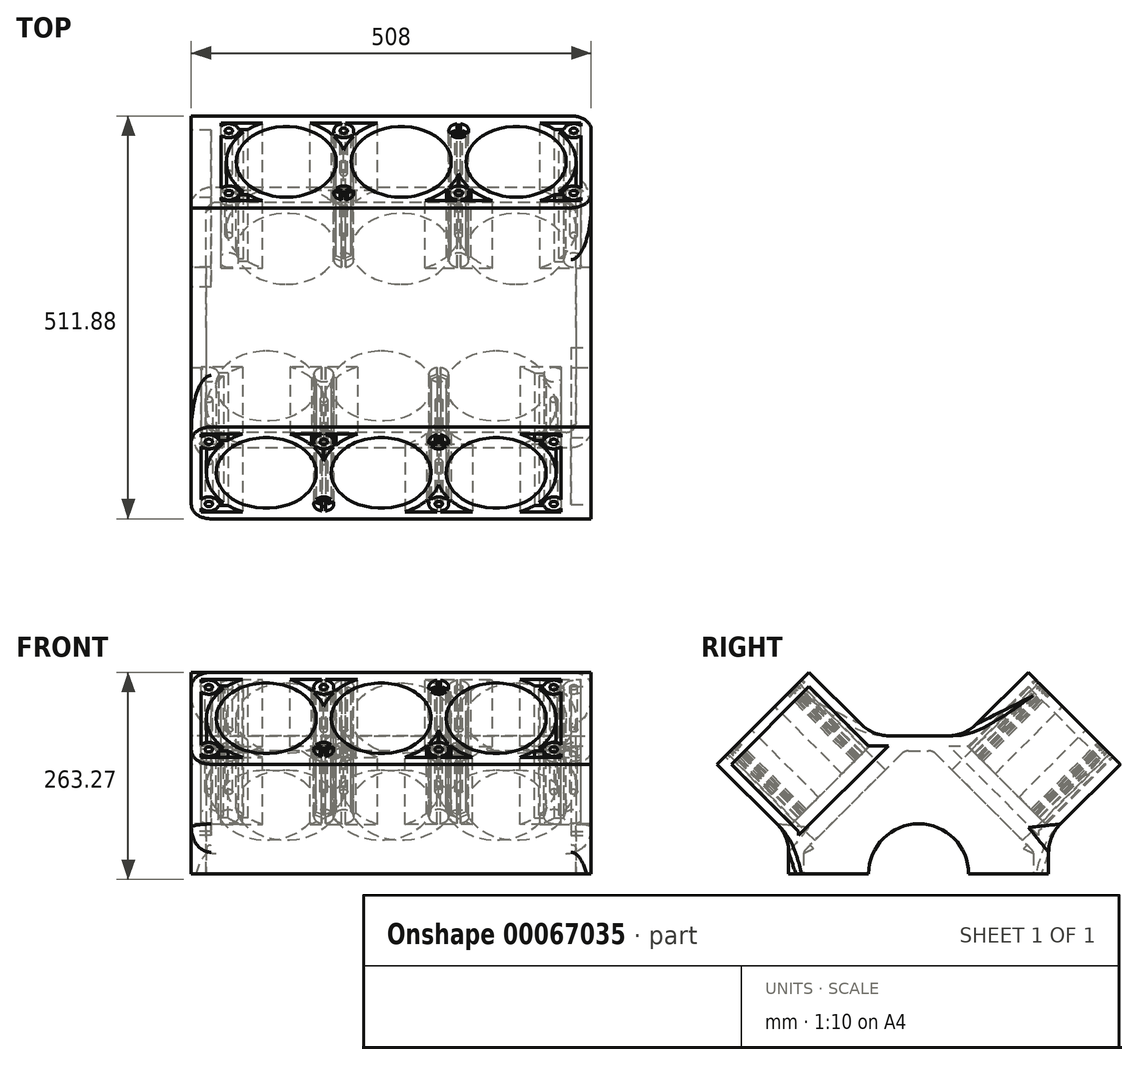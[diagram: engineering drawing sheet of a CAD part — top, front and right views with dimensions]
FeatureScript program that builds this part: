
annotation { "Feature Type Name" : "Feature", "Feature Type Description" : "" }
export const myFeature = defineFeature(function(context is Context, id is Id, definition is map)
    precondition{}
    {
        {
            var Q0;
            Q0=qCreatedBy(makeId("Right.planeOp"),FACE);
            var sketch = newSketch(context, id + "F0", { "sketchPlane" : qUnion([Q0])});
            skLineSegment(sketch, "E0", {"start": v(0, 175.36) * mm, "end": v(0, 0) * mm, "construction": true});
            skLineSegment(sketch, "E1", {"start": v(0, 0) * mm, "end": v(197.57, 197.57) * mm, "construction": true});
            skLineSegment(sketch, "E2", {"start": v(0, 175.36) * mm, "end": v(58.61, 175.36) * mm});
            skLineSegment(sketch, "E3", {"start": v(58.61, 175.36) * mm, "end": v(139.2, 255.94) * mm});
            skLineSegment(sketch, "E4", {"start": v(139.2, 255.94) * mm, "end": v(255.94, 139.2) * mm});
            skLineSegment(sketch, "E5", {"start": v(255.94, 139.2) * mm, "end": v(165.1, 48.36) * mm});
            skLineSegment(sketch, "E6", {"start": v(165.1, 48.36) * mm, "end": v(165.1, 0) * mm});
            skLineSegment(sketch, "E7", {"start": v(63.5, 0) * mm, "end": v(165.1, 0) * mm});
            skArc(sketch, "E8", {"start": v(0, 63.5) * mm, "mid": v(44.9, 44.9) * mm, "end": v(63.5, 0) * mm});
            skLineSegment(sketch, "E9", {"start": v(0, 175.36) * mm, "end": v(0, 63.5) * mm});
            skSolve(sketch);
        }
        {
            var Q0;
            Q0=qSketchRegion(id+"F0",true);
            extrude(context, id + "F1", {"entities" : qUnion([Q0]), "endBound" : BoundingType.SYMMETRIC, "depth" : 482.6 * mm});
        }
        {
            var Q0;
            Q0=makeQuery(id+"F1.opExtrude","SWEPT_FACE",FACE,{"disambiguationData":[OSD([sQuery(id+"F0.wireOp",EDGE,"E4")])]});
            var sketch = newSketch(context, id + "F2", { "sketchPlane" : qUnion([Q0])});
            skLineSegment(sketch, "E10", {"start": v(146.05, 0) * mm, "end": v(-146.05, 0) * mm, "construction": true});
            skCircle(sketch, "E11", {"center": v(146.05, 0) * mm, "radius": 63.5 * mm});
            skCircle(sketch, "E12", {"center": v(0, 0) * mm, "radius": 63.5 * mm});
            skCircle(sketch, "E13", {"center": v(-146.05, 0) * mm, "radius": 63.5 * mm});
            skSolve(sketch);
        }
        {
            var Q0;
            Q0=qSketchRegion(id+"F2",true);
            extrude(context, id + "F3", {"entities" : qUnion([Q0]), "operationType" : NewBodyOperationType.REMOVE, "endBound" : BoundingType.THROUGH_ALL, "oppositeDirection" : true, "depth" : 25.4 * mm});
        }
        {
            var Q0;
            Q0=makeQuery(id+"F1.opExtrude","SWEPT_FACE",FACE,{"disambiguationData":[OSD([sQuery(id+"F0.wireOp",EDGE,"E4")])]});
            var sketch = newSketch(context, id + "F4", { "sketchPlane" : qUnion([Q0])});
            skCircle(sketch, "E14", {"center": v(146.05, 0) * mm, "radius": 76 * mm});
            skCircle(sketch, "E15", {"center": v(0, 0) * mm, "radius": 76 * mm});
            skCircle(sketch, "E16", {"center": v(146.05, 0) * mm, "radius": 91.95 * mm, "construction": true});
            skCircle(sketch, "E17", {"center": v(73.03, -55.88) * mm, "radius": 12.7 * mm});
            skLineSegment(sketch, "E18", {"start": v(146.05, 0) * mm, "end": v(146.05, -169.57) * mm, "construction": true});
            skLineSegment(sketch, "E19", {"start": v(146.05, 0) * mm, "end": v(35.62, 0) * mm, "construction": true});
            skCircle(sketch, "E20.MirrorC", {"center": v(219.07, -55.88) * mm, "radius": 12.7 * mm});
            skCircle(sketch, "E21.MirrorC", {"center": v(73.03, 55.88) * mm, "radius": 12.7 * mm});
            skCircle(sketch, "E22.MirrorC", {"center": v(219.07, 55.88) * mm, "radius": 12.7 * mm});
            skLineSegment(sketch, "E23.bottom", {"start": v(228.6, -69.85) * mm, "end": v(-228.6, -69.85) * mm});
            skLineSegment(sketch, "E23.top", {"start": v(228.6, 69.85) * mm, "end": v(-228.6, 69.85) * mm});
            skLineSegment(sketch, "E23.left", {"start": v(228.6, -69.85) * mm, "end": v(228.6, 69.85) * mm});
            skLineSegment(sketch, "E23.right", {"start": v(-228.6, -69.85) * mm, "end": v(-228.6, 69.85) * mm});
            skLineSegment(sketch, "E24", {"start": v(0, -135.82) * mm, "end": v(0, 167.5) * mm, "construction": true});
            skCircle(sketch, "E25.MirrorC", {"center": v(-73.03, -55.88) * mm, "radius": 12.7 * mm});
            skCircle(sketch, "E26.MirrorC", {"center": v(-73.03, 55.88) * mm, "radius": 12.7 * mm});
            skCircle(sketch, "E27.MirrorC", {"center": v(-219.07, 55.88) * mm, "radius": 12.7 * mm});
            skCircle(sketch, "E28.MirrorC", {"center": v(-219.07, -55.88) * mm, "radius": 12.7 * mm});
            skCircle(sketch, "E29.MirrorC", {"center": v(-146.05, 0) * mm, "radius": 76 * mm});
            skSolve(sketch);
        }
        {
            var Q0;
            {var subQ9=sQuery(id+"F4.wireOp",EDGE,"E14");var subQ11=sQuery(id+"F4.wireOp",EDGE,"E23.top");var subQ12=makeQuery(id+"F4.imprint","INTERSECT",VERTEX,{"disambiguationData":[OD(1.0)],"derivedFrom":[subQ9,subQ11]});Q0=makeQuery(id+"F4.imprint","IMPRINT",FACE,{"disambiguationData":[TD([[makeQuery(id+"F4.imprint","IMPRINT",EDGE,{"disambiguationData":[TD([[subQ12,1.0]])],"derivedFrom":subQ9}),-1.0]])]});}
            var Q1;
            Q1=makeQuery(id+"F4.imprint","IMPRINT",FACE,{"disambiguationData":[TD([[makeQuery(id+"F4.imprint","IMPRINT",EDGE,{"derivedFrom":sQuery(id+"F4.wireOp",EDGE,"E17")}),-1.0]])]});
            var Q2;
            Q2=makeQuery(id+"F4.imprint","IMPRINT",FACE,{"disambiguationData":[TD([[makeQuery(id+"F4.imprint","IMPRINT",EDGE,{"derivedFrom":sQuery(id+"F4.wireOp",EDGE,"E21.MirrorC")}),1.0]])]});
            var Q3;
            Q3=makeQuery(id+"F4.imprint","IMPRINT",FACE,{"disambiguationData":[TD([[makeQuery(id+"F4.imprint","IMPRINT",EDGE,{"derivedFrom":sQuery(id+"F4.wireOp",EDGE,"E26.MirrorC")}),-1.0]])]});
            var Q4;
            Q4=makeQuery(id+"F4.imprint","IMPRINT",FACE,{"disambiguationData":[TD([[makeQuery(id+"F4.imprint","IMPRINT",EDGE,{"derivedFrom":sQuery(id+"F4.wireOp",EDGE,"E25.MirrorC")}),1.0]])]});
            var Q5;
            {var subQ0=sQuery(id+"F4.wireOp",EDGE,"E23.right");var subQ1=sQuery(id+"F4.wireOp",EDGE,"E23.bottom");var subQ2=makeQuery(id+"F4.imprint","INTERSECT",VERTEX,{"derivedFrom":[subQ1,subQ0]});Q5=makeQuery(id+"F4.imprint","IMPRINT",FACE,{"disambiguationData":[TD([[makeQuery(id+"F4.imprint","IMPRINT",EDGE,{"disambiguationData":[TD([[subQ2,1.0]])],"derivedFrom":subQ1}),-1.0]])]});}
            extrude(context, id + "F5", {"entities" : qUnion([Q0, Q1, Q2, Q3, Q4, Q5]), "operationType" : NewBodyOperationType.REMOVE, "oppositeDirection" : true, "depth" : 120.65 * mm});
        }
        {
            var Q0;
            {var subQ10=sQuery(id+"F0.wireOp",EDGE,"E4");var subQ11=sQuery(id+"F0.wireOp",EDGE,"E3");Q0=makeQuery(id+"F5.boolean.opBoolean","SPLIT",FACE,{"disambiguationData":[TD([makeQuery(id+"F1.opExtrude","SWEPT_FACE",FACE,{"disambiguationData":[OSD([subQ11])]})])],"derivedFrom":makeQuery(id+"F1.opExtrude","SWEPT_FACE",FACE,{"disambiguationData":[OSD([subQ10])]})});}
            var sketch = newSketch(context, id + "F6", { "sketchPlane" : qUnion([Q0])});
            skLineSegment(sketch, "E30", {"start": v(0, -135.93) * mm, "end": v(0, 142.24) * mm, "construction": true});
            skLineSegment(sketch, "E31", {"start": v(261.24, 0) * mm, "end": v(-274.05, 0) * mm, "construction": true});
            skLineSegment(sketch, "E32", {"start": v(70.53, 57.32) * mm, "end": v(70.53, 70.73) * mm});
            skLineSegment(sketch, "E33", {"start": v(73.03, 55.88) * mm, "end": v(88.64, 46.86) * mm, "construction": true});
            skLineSegment(sketch, "E34", {"start": v(73.03, 46.39) * mm, "end": v(73.03, 55.88) * mm, "construction": true});
            skPoint(sketch, "E35", {"position": v(73.03, 55.88) * mm});
            skLineSegment(sketch, "E36", {"start": v(89.9, 49.03) * mm, "end": v(75.53, 57.32) * mm});
            skLineSegment(sketch, "E37", {"start": v(73.03, 53) * mm, "end": v(59.03, 44.91) * mm});
            skLineSegment(sketch, "E38", {"start": v(73.03, 55.88) * mm, "end": v(57.78, 47.08) * mm, "construction": true});
            skLineSegment(sketch, "E39", {"start": v(75.53, 57.32) * mm, "end": v(75.53, 70.73) * mm});
            skLineSegment(sketch, "E40", {"start": v(56.53, 49.24) * mm, "end": v(70.53, 57.32) * mm});
            skLineSegment(sketch, "E41", {"start": v(87.4, 44.7) * mm, "end": v(73.03, 53) * mm});
            skLineSegment(sketch, "E42", {"start": v(70.53, 70.73) * mm, "end": v(70.53, 57.32) * mm, "construction": true});
            skLineSegment(sketch, "E43", {"start": v(59.03, 44.91) * mm, "end": v(56.53, 49.24) * mm});
            skLineSegment(sketch, "E44", {"start": v(87.4, 44.7) * mm, "end": v(89.9, 49.03) * mm});
            skLineSegment(sketch, "E45", {"start": v(75.53, 70.73) * mm, "end": v(70.53, 70.73) * mm});
            skLineSegment(sketch, "E46", {"start": v(75.53, 70.73) * mm, "end": v(70.53, 70.73) * mm, "construction": true});
            skLineSegment(sketch, "E47.MirrorCS", {"start": v(89.9, -49.03) * mm, "end": v(75.53, -57.32) * mm});
            skLineSegment(sketch, "E48.MirrorCS", {"start": v(87.4, -44.7) * mm, "end": v(73.03, -53) * mm});
            skLineSegment(sketch, "E49.MirrorCS", {"start": v(73.03, -53) * mm, "end": v(59.03, -44.91) * mm});
            skLineSegment(sketch, "E50.MirrorCS", {"start": v(59.03, -44.91) * mm, "end": v(56.53, -49.24) * mm});
            skLineSegment(sketch, "E51.MirrorCS", {"start": v(56.53, -49.24) * mm, "end": v(70.53, -57.32) * mm});
            skLineSegment(sketch, "E52.MirrorCS", {"start": v(70.53, -57.32) * mm, "end": v(70.53, -70.73) * mm});
            skLineSegment(sketch, "E53.MirrorCS", {"start": v(75.53, -70.73) * mm, "end": v(70.53, -70.73) * mm});
            skLineSegment(sketch, "E54.MirrorCS", {"start": v(75.53, -57.32) * mm, "end": v(75.53, -70.73) * mm});
            skLineSegment(sketch, "E55.MirrorCS", {"start": v(87.4, -44.7) * mm, "end": v(89.9, -49.03) * mm});
            skLineSegment(sketch, "E56.MirrorCS", {"start": v(-87.4, 44.7) * mm, "end": v(-89.9, 49.03) * mm});
            skLineSegment(sketch, "E57.MirrorCS", {"start": v(-87.4, 44.7) * mm, "end": v(-73.03, 53) * mm});
            skLineSegment(sketch, "E58.MirrorCS", {"start": v(-73.03, 53) * mm, "end": v(-59.03, 44.91) * mm});
            skLineSegment(sketch, "E59.MirrorCS", {"start": v(-59.03, 44.91) * mm, "end": v(-56.53, 49.24) * mm});
            skLineSegment(sketch, "E60.MirrorCS", {"start": v(-56.53, 49.24) * mm, "end": v(-70.53, 57.32) * mm});
            skLineSegment(sketch, "E61.MirrorCS", {"start": v(-70.53, 57.32) * mm, "end": v(-70.53, 70.73) * mm});
            skLineSegment(sketch, "E62.MirrorCS", {"start": v(-75.53, 70.73) * mm, "end": v(-70.53, 70.73) * mm});
            skLineSegment(sketch, "E63.MirrorCS", {"start": v(-75.53, 57.32) * mm, "end": v(-75.53, 70.73) * mm});
            skLineSegment(sketch, "E64.MirrorCS", {"start": v(-89.9, 49.03) * mm, "end": v(-75.53, 57.32) * mm});
            skLineSegment(sketch, "E65.MirrorCS", {"start": v(-59.03, -44.91) * mm, "end": v(-56.53, -49.24) * mm});
            skLineSegment(sketch, "E66.MirrorCS", {"start": v(-73.03, -53) * mm, "end": v(-59.03, -44.91) * mm});
            skLineSegment(sketch, "E67.MirrorCS", {"start": v(-87.4, -44.7) * mm, "end": v(-73.03, -53) * mm});
            skLineSegment(sketch, "E68.MirrorCS", {"start": v(-87.4, -44.7) * mm, "end": v(-89.9, -49.03) * mm});
            skLineSegment(sketch, "E69.MirrorCS", {"start": v(-89.9, -49.03) * mm, "end": v(-75.53, -57.32) * mm});
            skLineSegment(sketch, "E70.MirrorCS", {"start": v(-75.53, -57.32) * mm, "end": v(-75.53, -70.73) * mm});
            skLineSegment(sketch, "E71.MirrorCS", {"start": v(-75.53, -70.73) * mm, "end": v(-70.53, -70.73) * mm});
            skLineSegment(sketch, "E72.MirrorCS", {"start": v(-70.53, -57.32) * mm, "end": v(-70.53, -70.73) * mm});
            skLineSegment(sketch, "E73.MirrorCS", {"start": v(-56.53, -49.24) * mm, "end": v(-70.53, -57.32) * mm});
            skLineSegment(sketch, "E74", {"start": v(206.37, -55.88) * mm, "end": v(197.56, -55.88) * mm, "construction": true});
            skLineSegment(sketch, "E75", {"start": v(209.05, -58.38) * mm, "end": v(209.05, -53.38) * mm});
            skLineSegment(sketch, "E76", {"start": v(209.05, -53.38) * mm, "end": v(192.06, -53.38) * mm});
            skLineSegment(sketch, "E77", {"start": v(192.06, -53.38) * mm, "end": v(192.06, -58.38) * mm});
            skLineSegment(sketch, "E78", {"start": v(192.06, -58.38) * mm, "end": v(209.05, -58.38) * mm});
            skLineSegment(sketch, "E79.MirrorCS", {"start": v(-209.05, -58.38) * mm, "end": v(-209.05, -53.38) * mm});
            skLineSegment(sketch, "E80.MirrorCS", {"start": v(-192.06, -58.38) * mm, "end": v(-209.05, -58.38) * mm});
            skLineSegment(sketch, "E81.MirrorCS", {"start": v(-192.06, -53.38) * mm, "end": v(-192.06, -58.38) * mm});
            skLineSegment(sketch, "E82.MirrorCS", {"start": v(-209.05, -53.38) * mm, "end": v(-192.06, -53.38) * mm});
            skLineSegment(sketch, "E83.MirrorCS", {"start": v(209.05, 58.38) * mm, "end": v(209.05, 53.38) * mm});
            skLineSegment(sketch, "E84.MirrorCS", {"start": v(192.06, 58.38) * mm, "end": v(209.05, 58.38) * mm});
            skLineSegment(sketch, "E85.MirrorCS", {"start": v(209.05, 53.38) * mm, "end": v(192.06, 53.38) * mm});
            skLineSegment(sketch, "E86.MirrorCS", {"start": v(192.06, 53.38) * mm, "end": v(192.06, 58.38) * mm});
            skLineSegment(sketch, "E87.MirrorCS", {"start": v(-209.05, 53.38) * mm, "end": v(-192.06, 53.38) * mm});
            skLineSegment(sketch, "E88.MirrorCS", {"start": v(-192.06, 53.38) * mm, "end": v(-192.06, 58.38) * mm});
            skLineSegment(sketch, "E89.MirrorCS", {"start": v(-192.06, 58.38) * mm, "end": v(-209.05, 58.38) * mm});
            skLineSegment(sketch, "E90.MirrorCS", {"start": v(-209.05, 58.38) * mm, "end": v(-209.05, 53.38) * mm});
            skSolve(sketch);
        }
        {
            var Q0;
            Q0=qSketchRegion(id+"F6",true);
            extrude(context, id + "F7", {"entities" : qUnion([Q0]), "operationType" : NewBodyOperationType.ADD, "oppositeDirection" : true, "depth" : 120.65 * mm});
        }
        {
            var Q0;
            {var subQ26=sQuery(id+"F0.wireOp",EDGE,"E3");var subQ32=sQuery(id+"F0.wireOp",EDGE,"E4");Q0=makeQuery(id+"F5.boolean.opBoolean","SPLIT",FACE,{"disambiguationData":[TD([makeQuery(id+"F1.opExtrude","SWEPT_FACE",FACE,{"disambiguationData":[OSD([subQ26])]})])],"derivedFrom":makeQuery(id+"F1.opExtrude","SWEPT_FACE",FACE,{"disambiguationData":[OSD([subQ32])]})});}
            var sketch = newSketch(context, id + "F8", { "sketchPlane" : qUnion([Q0])});
            skCircle(sketch, "E91", {"center": v(219.07, 55.88) * mm, "radius": 4.76 * mm});
            skCircle(sketch, "E92", {"center": v(73.03, 55.88) * mm, "radius": 4.76 * mm});
            skLineSegment(sketch, "E93", {"start": v(0, -161.36) * mm, "end": v(0, 186.57) * mm, "construction": true});
            skLineSegment(sketch, "E94", {"start": v(291.36, 0) * mm, "end": v(-286.68, 0) * mm, "construction": true});
            skCircle(sketch, "E95.MirrorC", {"center": v(219.07, -55.88) * mm, "radius": 4.76 * mm});
            skCircle(sketch, "E96.MirrorC", {"center": v(73.03, -55.88) * mm, "radius": 4.76 * mm});
            skCircle(sketch, "E97.MirrorC", {"center": v(-73.03, -55.88) * mm, "radius": 4.76 * mm});
            skCircle(sketch, "E98.MirrorC", {"center": v(-73.03, 55.88) * mm, "radius": 4.76 * mm});
            skCircle(sketch, "E99.MirrorC", {"center": v(-219.07, -55.88) * mm, "radius": 4.76 * mm});
            skCircle(sketch, "E100.MirrorC", {"center": v(-219.07, 55.88) * mm, "radius": 4.76 * mm});
            skSolve(sketch);
        }
        {
            var Q0;
            Q0=qSketchRegion(id+"F8",true);
            extrude(context, id + "F9", {"entities" : qUnion([Q0]), "operationType" : NewBodyOperationType.REMOVE, "oppositeDirection" : true, "depth" : 76 * mm});
        }
        {
            var Q0;
            Q0=qCreatedBy(makeId("Front.planeOp"),FACE);
            var sketch = newSketch(context, id + "F10", { "sketchPlane" : qUnion([Q0])});
            skLineSegment(sketch, "E101", {"start": v(-12.7, 175.36) * mm, "end": v(-12.7, 131) * mm, "construction": true});
            skSolve(sketch);
        }
        {
            var Q0;
            Q0=makeQuery(id+"F1.opExtrude","SWEPT_BODY",BODY,{"disambiguationData":[OSD([sQuery(id+"F0.wireOp",EDGE,"E2"),sQuery(id+"F0.wireOp",EDGE,"E3"),sQuery(id+"F0.wireOp",EDGE,"E4"),sQuery(id+"F0.wireOp",EDGE,"E5"),sQuery(id+"F0.wireOp",EDGE,"E6"),sQuery(id+"F0.wireOp",EDGE,"E7"),sQuery(id+"F0.wireOp",EDGE,"E8"),sQuery(id+"F0.wireOp",EDGE,"E9")])]});
            var Q1;
            Q1=sQuery(id+"F10.wireOp",EDGE,"E101");
            circularPattern(context, id + "F11", {"entities" : qUnion([Q0]), "axis" : qUnion([Q1]), "angle" : 180 * degree, "instanceCount" : 2});
        }
        {
            var Q0;
            Q0=makeQuery(id+"F11.opPattern","COPY",FACE,{"derivedFrom":makeQuery(id+"F1.opExtrude","CAP_FACE",FACE,{"disambiguationData":[OSD([sQuery(id+"F0.wireOp",EDGE,"E2"),sQuery(id+"F0.wireOp",EDGE,"E3"),sQuery(id+"F0.wireOp",EDGE,"E4"),sQuery(id+"F0.wireOp",EDGE,"E5"),sQuery(id+"F0.wireOp",EDGE,"E6"),sQuery(id+"F0.wireOp",EDGE,"E7"),sQuery(id+"F0.wireOp",EDGE,"E8"),sQuery(id+"F0.wireOp",EDGE,"E9")])],"isStart":true}),"instanceName":"1"});
            var sketch = newSketch(context, id + "F12", { "sketchPlane" : qUnion([Q0])});
            skLineSegment(sketch, "E102.0", {"start": v(-139.2, 255.94) * mm, "end": v(-255.94, 139.2) * mm});
            skLineSegment(sketch, "E103.0", {"start": v(-58.61, 175.36) * mm, "end": v(-139.2, 255.94) * mm});
            skLineSegment(sketch, "E104.0", {"start": v(0, 175.36) * mm, "end": v(-58.61, 175.36) * mm});
            skLineSegment(sketch, "E105.0", {"start": v(-255.94, 139.2) * mm, "end": v(-165.1, 48.36) * mm});
            skLineSegment(sketch, "E106.0", {"start": v(-165.1, 48.36) * mm, "end": v(-165.1, 0) * mm});
            skLineSegment(sketch, "E107.0", {"start": v(-63.5, 0) * mm, "end": v(-165.1, 0) * mm});
            skArc(sketch, "E108.0", {"start": v(0, 63.5) * mm, "mid": v(-44.9, 44.9) * mm, "end": v(-63.5, 0) * mm});
            skLineSegment(sketch, "E109.0", {"start": v(0, 175.36) * mm, "end": v(0, 63.5) * mm});
            skSolve(sketch);
        }
        {
            var Q0;
            Q0=qSketchRegion(id+"F12",true);
            var Q1;
            Q1=makeQuery(id+"F1.opExtrude","CAP_FACE",FACE,{"disambiguationData":[OSD([sQuery(id+"F0.wireOp",EDGE,"E2"),sQuery(id+"F0.wireOp",EDGE,"E3"),sQuery(id+"F0.wireOp",EDGE,"E4"),sQuery(id+"F0.wireOp",EDGE,"E5"),sQuery(id+"F0.wireOp",EDGE,"E6"),sQuery(id+"F0.wireOp",EDGE,"E7"),sQuery(id+"F0.wireOp",EDGE,"E8"),sQuery(id+"F0.wireOp",EDGE,"E9")])],"isStart":false});
            extrude(context, id + "F13", {"entities" : qUnion([Q0]), "operationType" : NewBodyOperationType.ADD, "endBound" : BoundingType.UP_TO_SURFACE, "endBoundEntityFace" : qUnion([Q1]), "depth" : 25.4 * mm});
        }
        {
            var Q0;
            Q0=makeQuery(id+"F1.opExtrude","CAP_FACE",FACE,{"disambiguationData":[OSD([sQuery(id+"F0.wireOp",EDGE,"E2"),sQuery(id+"F0.wireOp",EDGE,"E3"),sQuery(id+"F0.wireOp",EDGE,"E4"),sQuery(id+"F0.wireOp",EDGE,"E5"),sQuery(id+"F0.wireOp",EDGE,"E6"),sQuery(id+"F0.wireOp",EDGE,"E7"),sQuery(id+"F0.wireOp",EDGE,"E8"),sQuery(id+"F0.wireOp",EDGE,"E9")])],"isStart":true});
            var sketch = newSketch(context, id + "F14", { "sketchPlane" : qUnion([Q0])});
            skLineSegment(sketch, "E110.0", {"start": v(-58.61, 175.36) * mm, "end": v(-139.2, 255.94) * mm});
            skLineSegment(sketch, "E111.0", {"start": v(-139.2, 255.94) * mm, "end": v(-255.94, 139.2) * mm});
            skLineSegment(sketch, "E112.0", {"start": v(-255.94, 139.2) * mm, "end": v(-165.1, 48.36) * mm});
            skLineSegment(sketch, "E113.0", {"start": v(-165.1, 48.36) * mm, "end": v(-165.1, 0) * mm});
            skLineSegment(sketch, "E114.0", {"start": v(-63.5, 0) * mm, "end": v(-165.1, 0) * mm});
            skArc(sketch, "E115.0", {"start": v(0, 63.5) * mm, "mid": v(-44.9, 44.9) * mm, "end": v(-63.5, 0) * mm});
            skLineSegment(sketch, "E116.0", {"start": v(0, 175.36) * mm, "end": v(-58.61, 175.36) * mm});
            skLineSegment(sketch, "E117.0", {"start": v(0, 175.36) * mm, "end": v(0, 63.5) * mm});
            skSolve(sketch);
        }
        {
            var Q0;
            Q0=qSketchRegion(id+"F14",true);
            var Q1;
            Q1=makeQuery(id+"F11.opPattern","COPY",FACE,{"derivedFrom":makeQuery(id+"F1.opExtrude","CAP_FACE",FACE,{"disambiguationData":[OSD([sQuery(id+"F0.wireOp",EDGE,"E2"),sQuery(id+"F0.wireOp",EDGE,"E3"),sQuery(id+"F0.wireOp",EDGE,"E4"),sQuery(id+"F0.wireOp",EDGE,"E5"),sQuery(id+"F0.wireOp",EDGE,"E6"),sQuery(id+"F0.wireOp",EDGE,"E7"),sQuery(id+"F0.wireOp",EDGE,"E8"),sQuery(id+"F0.wireOp",EDGE,"E9")])],"isStart":false}),"instanceName":"1"});
            extrude(context, id + "F15", {"entities" : qUnion([Q0]), "operationType" : NewBodyOperationType.ADD, "endBound" : BoundingType.UP_TO_SURFACE, "endBoundEntityFace" : qUnion([Q1]), "depth" : 25.4 * mm});
        }
        {
            var Q0;
            Q0=makeQuery(id+"F13.boolean.opBoolean","MERGE",FACE,{"derivedFrom":[makeQuery(id+"F1.opExtrude","CAP_FACE",FACE,{"disambiguationData":[OSD([sQuery(id+"F0.wireOp",EDGE,"E2"),sQuery(id+"F0.wireOp",EDGE,"E3"),sQuery(id+"F0.wireOp",EDGE,"E4"),sQuery(id+"F0.wireOp",EDGE,"E5"),sQuery(id+"F0.wireOp",EDGE,"E6"),sQuery(id+"F0.wireOp",EDGE,"E7"),sQuery(id+"F0.wireOp",EDGE,"E8"),sQuery(id+"F0.wireOp",EDGE,"E9")])],"isStart":false}),makeQuery(id+"F13.opExtrude","CAP_FACE",FACE,{"disambiguationData":[OSD([sQuery(id+"F12.wireOp",EDGE,"E102.0"),sQuery(id+"F12.wireOp",EDGE,"E103.0"),sQuery(id+"F12.wireOp",EDGE,"E104.0"),sQuery(id+"F12.wireOp",EDGE,"E105.0"),sQuery(id+"F12.wireOp",EDGE,"E106.0"),sQuery(id+"F12.wireOp",EDGE,"E107.0"),sQuery(id+"F12.wireOp",EDGE,"E108.0"),sQuery(id+"F12.wireOp",EDGE,"E109.0")])],"isStart":false})]});
            var sketch = newSketch(context, id + "F16", { "sketchPlane" : qUnion([Q0])});
            skLineSegment(sketch, "E118.0", {"start": v(139.2, 237.98) * mm, "end": v(63.87, 162.66) * mm});
            skLineSegment(sketch, "E118.1", {"start": v(-152.4, 53.62) * mm, "end": v(-152.4, 12.7) * mm});
            skLineSegment(sketch, "E118.2", {"start": v(-237.98, 139.2) * mm, "end": v(-152.4, 53.62) * mm});
            skLineSegment(sketch, "E118.3", {"start": v(-139.2, 237.98) * mm, "end": v(-237.98, 139.2) * mm});
            skLineSegment(sketch, "E118.4", {"start": v(-63.87, 162.66) * mm, "end": v(-139.2, 237.98) * mm});
            skLineSegment(sketch, "E118.5", {"start": v(-152.4, 12.7) * mm, "end": v(-75.13, 12.7) * mm});
            skLineSegment(sketch, "E118.6", {"start": v(63.87, 162.66) * mm, "end": v(-63.87, 162.66) * mm});
            skArc(sketch, "E118.7", {"start": v(-75.13, 12.7) * mm, "mid": v(0, 76.2) * mm, "end": v(75.13, 12.7) * mm});
            skLineSegment(sketch, "E118.8", {"start": v(75.13, 12.7) * mm, "end": v(152.4, 12.7) * mm});
            skLineSegment(sketch, "E118.9", {"start": v(152.4, 12.7) * mm, "end": v(152.4, 53.62) * mm});
            skLineSegment(sketch, "E118.10", {"start": v(152.4, 53.62) * mm, "end": v(237.98, 139.2) * mm});
            skLineSegment(sketch, "E118.11", {"start": v(237.98, 139.2) * mm, "end": v(139.2, 237.98) * mm});
            skLineSegment(sketch, "E119", {"start": v(-38.36, 162.66) * mm, "end": v(-152.4, 48.62) * mm});
            skLineSegment(sketch, "E120", {"start": v(-152.4, 53.62) * mm, "end": v(-152.4, 48.62) * mm});
            skSolve(sketch);
        }
        {
            var Q0;
            Q0=makeQuery(id+"F16.imprint","IMPRINT",FACE,{"disambiguationData":[TD([[makeQuery(id+"F16.imprint","IMPRINT",EDGE,{"derivedFrom":sQuery(id+"F16.wireOp",EDGE,"E118.2")}),1.0]])]});
            extrude(context, id + "F17", {"entities" : qUnion([Q0]), "operationType" : NewBodyOperationType.REMOVE, "oppositeDirection" : true, "depth" : 25.4 * mm});
        }
        {
            var Q0;
            Q0=makeQuery(id+"F15.boolean.opBoolean","MERGE",FACE,{"derivedFrom":[makeQuery(id+"F11.opPattern","COPY",FACE,{"derivedFrom":makeQuery(id+"F1.opExtrude","CAP_FACE",FACE,{"disambiguationData":[OSD([sQuery(id+"F0.wireOp",EDGE,"E2"),sQuery(id+"F0.wireOp",EDGE,"E3"),sQuery(id+"F0.wireOp",EDGE,"E4"),sQuery(id+"F0.wireOp",EDGE,"E5"),sQuery(id+"F0.wireOp",EDGE,"E6"),sQuery(id+"F0.wireOp",EDGE,"E7"),sQuery(id+"F0.wireOp",EDGE,"E8"),sQuery(id+"F0.wireOp",EDGE,"E9")])],"isStart":false}),"instanceName":"1"}),makeQuery(id+"F15.opExtrude","CAP_FACE",FACE,{"disambiguationData":[OSD([sQuery(id+"F14.wireOp",EDGE,"E110.0"),sQuery(id+"F14.wireOp",EDGE,"E111.0"),sQuery(id+"F14.wireOp",EDGE,"E112.0"),sQuery(id+"F14.wireOp",EDGE,"E113.0"),sQuery(id+"F14.wireOp",EDGE,"E114.0"),sQuery(id+"F14.wireOp",EDGE,"E115.0"),sQuery(id+"F14.wireOp",EDGE,"E116.0"),sQuery(id+"F14.wireOp",EDGE,"E117.0")])],"isStart":false})]});
            var sketch = newSketch(context, id + "F18", { "sketchPlane" : qUnion([Q0])});
            skLineSegment(sketch, "E121.0", {"start": v(139.2, 237.98) * mm, "end": v(63.87, 162.66) * mm});
            skLineSegment(sketch, "E121.1", {"start": v(-152.4, 53.62) * mm, "end": v(-152.4, 12.7) * mm});
            skLineSegment(sketch, "E121.2", {"start": v(-237.98, 139.2) * mm, "end": v(-152.4, 53.62) * mm});
            skLineSegment(sketch, "E121.3", {"start": v(-139.2, 237.98) * mm, "end": v(-237.98, 139.2) * mm});
            skLineSegment(sketch, "E121.4", {"start": v(-63.87, 162.66) * mm, "end": v(-139.2, 237.98) * mm});
            skLineSegment(sketch, "E121.5", {"start": v(-152.4, 12.7) * mm, "end": v(-75.13, 12.7) * mm});
            skLineSegment(sketch, "E121.6", {"start": v(63.87, 162.66) * mm, "end": v(-63.87, 162.66) * mm});
            skArc(sketch, "E121.7", {"start": v(-75.13, 12.7) * mm, "mid": v(0, 76.2) * mm, "end": v(75.13, 12.7) * mm});
            skLineSegment(sketch, "E121.8", {"start": v(75.13, 12.7) * mm, "end": v(152.4, 12.7) * mm});
            skLineSegment(sketch, "E121.9", {"start": v(152.4, 12.7) * mm, "end": v(152.4, 53.62) * mm});
            skLineSegment(sketch, "E121.10", {"start": v(152.4, 53.62) * mm, "end": v(237.98, 139.2) * mm});
            skLineSegment(sketch, "E121.11", {"start": v(237.98, 139.2) * mm, "end": v(139.2, 237.98) * mm});
            skLineSegment(sketch, "E122", {"start": v(-152.4, 48.62) * mm, "end": v(-38.36, 162.66) * mm});
            skSolve(sketch);
        }
        {
            var Q0;
            {var subQ0=sQuery(id+"F18.wireOp",EDGE,"E121.2");Q0=makeQuery(id+"F18.imprint","IMPRINT",FACE,{"disambiguationData":[TD([[makeQuery(id+"F18.imprint","IMPRINT",EDGE,{"derivedFrom":subQ0}),1.0]])]});}
            extrude(context, id + "F19", {"entities" : qUnion([Q0]), "operationType" : NewBodyOperationType.REMOVE, "oppositeDirection" : true, "depth" : 25.4 * mm});
        }
        {
            var Q0;
            Q0=qCreatedBy(makeId("Right.planeOp"),FACE);
            var sketch = newSketch(context, id + "F20", { "sketchPlane" : qUnion([Q0])});
            skLineSegment(sketch, "E123", {"start": v(0, 156.3) * mm, "end": v(0, -34.1) * mm, "construction": true});
            skLineSegment(sketch, "E124", {"start": v(0, 156.3) * mm, "end": v(-18, 156.3) * mm});
            skLineSegment(sketch, "E125", {"start": v(-18, 156.31) * mm, "end": v(-146.05, 28.26) * mm});
            skLineSegment(sketch, "E126", {"start": v(-146.05, 28.26) * mm, "end": v(-146.05, -34.1) * mm});
            skLineSegment(sketch, "E127", {"start": v(-146.05, -34.1) * mm, "end": v(0, -34.1) * mm});
            skLineSegment(sketch, "E128.MirrorCS", {"start": v(0, 156.3) * mm, "end": v(18, 156.3) * mm});
            skLineSegment(sketch, "E129.MirrorCS", {"start": v(18, 156.31) * mm, "end": v(146.05, 28.26) * mm});
            skLineSegment(sketch, "E130.MirrorCS", {"start": v(146.05, 28.26) * mm, "end": v(146.05, -34.1) * mm});
            skLineSegment(sketch, "E131.MirrorCS", {"start": v(146.05, -34.1) * mm, "end": v(0, -34.1) * mm});
            skSolve(sketch);
        }
        {
            var Q0;
            Q0=qSketchRegion(id+"F20",true);
            extrude(context, id + "F21", {"entities" : qUnion([Q0]), "operationType" : NewBodyOperationType.REMOVE, "depth" : 222.25 * mm, "hasSecondDirection" : true, "secondDirectionOppositeDirection" : true, "secondDirectionDepth" : 247.65 * mm});
        }
        {
            var Q0;
            Q0=makeQuery(id+"F21.boolean.opBoolean","COPY",EDGE,{"derivedFrom":makeQuery(id+"F21.opExtrude","CAP_EDGE",EDGE,{"disambiguationData":[OSD([sQuery(id+"F20.wireOp",EDGE,"E125")])],"isStart":true})});
            var Q1;
            Q1=makeQuery(id+"F21.boolean.opBoolean","COPY",EDGE,{"derivedFrom":makeQuery(id+"F21.opExtrude","CAP_EDGE",EDGE,{"disambiguationData":[OSD([sQuery(id+"F20.wireOp",EDGE,"E124"),sQuery(id+"F20.wireOp",EDGE,"E128.MirrorCS")])],"isStart":true})});
            var Q2;
            Q2=makeQuery(id+"F21.boolean.opBoolean","COPY",EDGE,{"derivedFrom":makeQuery(id+"F21.opExtrude","CAP_EDGE",EDGE,{"disambiguationData":[OSD([sQuery(id+"F20.wireOp",EDGE,"E129.MirrorCS")])],"isStart":true})});
            var Q3;
            Q3=makeQuery(id+"F21.boolean.opBoolean","COPY",EDGE,{"derivedFrom":makeQuery(id+"F21.opExtrude","SWEPT_EDGE",EDGE,{"disambiguationData":[OSD([sQuery(id+"F20.wireOp",EDGE,"E125"),sQuery(id+"F20.wireOp",EDGE,"E126")])]})});
            var Q4;
            Q4=makeQuery(id+"F21.boolean.opBoolean","COPY",EDGE,{"derivedFrom":makeQuery(id+"F21.opExtrude","CAP_EDGE",EDGE,{"disambiguationData":[OSD([sQuery(id+"F20.wireOp",EDGE,"E125")])],"isStart":false})});
            var Q5;
            Q5=makeQuery(id+"F21.boolean.opBoolean","COPY",EDGE,{"derivedFrom":makeQuery(id+"F21.opExtrude","CAP_EDGE",EDGE,{"disambiguationData":[OSD([sQuery(id+"F20.wireOp",EDGE,"E124"),sQuery(id+"F20.wireOp",EDGE,"E128.MirrorCS")])],"isStart":false})});
            var Q6;
            Q6=makeQuery(id+"F21.boolean.opBoolean","COPY",EDGE,{"derivedFrom":makeQuery(id+"F21.opExtrude","CAP_EDGE",EDGE,{"disambiguationData":[OSD([sQuery(id+"F20.wireOp",EDGE,"E129.MirrorCS")])],"isStart":false})});
            var Q7;
            Q7=makeQuery(id+"F21.boolean.opBoolean","COPY",EDGE,{"derivedFrom":makeQuery(id+"F21.opExtrude","SWEPT_EDGE",EDGE,{"disambiguationData":[OSD([sQuery(id+"F20.wireOp",EDGE,"E129.MirrorCS"),sQuery(id+"F20.wireOp",EDGE,"E130.MirrorCS")])]})});
            fillet(context, id + "F22", {"entities" : qUnion([Q0, Q1, Q2, Q3, Q4, Q5, Q6, Q7]), "radius" : 6.35 * mm, "tangentPropagation" : true, "allowEdgeOverflow" : false});
        }
        {
            var Q0;
            Q0=makeQuery(id+"F21.boolean.opBoolean","COPY",EDGE,{"derivedFrom":makeQuery(id+"F21.opExtrude","SWEPT_EDGE",EDGE,{"disambiguationData":[OSD([sQuery(id+"F20.wireOp",EDGE,"E128.MirrorCS"),sQuery(id+"F20.wireOp",EDGE,"E129.MirrorCS")])]})});
            var Q1;
            Q1=makeQuery(id+"F21.boolean.opBoolean","COPY",EDGE,{"derivedFrom":makeQuery(id+"F21.opExtrude","SWEPT_EDGE",EDGE,{"disambiguationData":[OSD([sQuery(id+"F20.wireOp",EDGE,"E124"),sQuery(id+"F20.wireOp",EDGE,"E125")])]})});
            var Q2;
            Q2=makeQuery(id+"F21.boolean.opBoolean","COPY",EDGE,{"derivedFrom":makeQuery(id+"F21.opExtrude","CAP_EDGE",EDGE,{"disambiguationData":[OSD([sQuery(id+"F20.wireOp",EDGE,"E126")])],"isStart":false})});
            var Q3;
            Q3=makeQuery(id+"F21.boolean.opBoolean","COPY",EDGE,{"derivedFrom":makeQuery(id+"F21.opExtrude","CAP_EDGE",EDGE,{"disambiguationData":[OSD([sQuery(id+"F20.wireOp",EDGE,"E130.MirrorCS")])],"isStart":false})});
            var Q4;
            Q4=makeQuery(id+"F21.boolean.opBoolean","COPY",EDGE,{"derivedFrom":makeQuery(id+"F21.opExtrude","CAP_EDGE",EDGE,{"disambiguationData":[OSD([sQuery(id+"F20.wireOp",EDGE,"E130.MirrorCS")])],"isStart":true})});
            var Q5;
            Q5=makeQuery(id+"F21.boolean.opBoolean","COPY",EDGE,{"derivedFrom":makeQuery(id+"F21.opExtrude","CAP_EDGE",EDGE,{"disambiguationData":[OSD([sQuery(id+"F20.wireOp",EDGE,"E126")])],"isStart":true})});
            fillet(context, id + "F23", {"entities" : qUnion([Q0, Q1, Q2, Q3, Q4, Q5]), "radius" : 12.7 * mm, "tangentPropagation" : true, "allowEdgeOverflow" : false});
        }
        {
            var Q0;
            Q0=makeQuery(id+"F11.opPattern","COPY",EDGE,{"derivedFrom":makeQuery(id+"F1.opExtrude","CAP_EDGE",EDGE,{"disambiguationData":[OSD([sQuery(id+"F0.wireOp",EDGE,"E5")])],"isStart":false}),"instanceName":"1"});
            var Q1;
            Q1=makeQuery(id+"F11.opPattern","COPY",EDGE,{"derivedFrom":makeQuery(id+"F1.opExtrude","CAP_EDGE",EDGE,{"disambiguationData":[OSD([sQuery(id+"F0.wireOp",EDGE,"E6")])],"isStart":false}),"instanceName":"1"});
            var Q2;
            Q2=makeQuery(id+"F11.opPattern","COPY",EDGE,{"derivedFrom":makeQuery(id+"F1.opExtrude","CAP_EDGE",EDGE,{"disambiguationData":[OSD([sQuery(id+"F0.wireOp",EDGE,"E3")])],"isStart":false}),"instanceName":"1"});
            var Q3;
            Q3=makeQuery(id+"F1.opExtrude","CAP_EDGE",EDGE,{"disambiguationData":[OSD([sQuery(id+"F0.wireOp",EDGE,"E6")])],"isStart":false});
            var Q4;
            Q4=makeQuery(id+"F1.opExtrude","CAP_EDGE",EDGE,{"disambiguationData":[OSD([sQuery(id+"F0.wireOp",EDGE,"E5")])],"isStart":false});
            var Q5;
            Q5=makeQuery(id+"F1.opExtrude","CAP_EDGE",EDGE,{"disambiguationData":[OSD([sQuery(id+"F0.wireOp",EDGE,"E3")])],"isStart":false});
            fillet(context, id + "F24", {"entities" : qUnion([Q0, Q1, Q2, Q3, Q4, Q5]), "radius" : 25.4 * mm, "tangentPropagation" : true, "allowEdgeOverflow" : false});
        }
        {
            var Q0;
            Q0=makeQuery(id+"F13.opExtrude","CAP_EDGE",EDGE,{"disambiguationData":[OSD([sQuery(id+"F12.wireOp",EDGE,"E106.0")])],"isStart":false});
            fillet(context, id + "F25", {"entities" : qUnion([Q0]), "radius" : 25.4 * mm, "tangentPropagation" : true, "allowEdgeOverflow" : false});
        }
        {
            var Q0;
            Q0=makeQuery(id+"F15.opExtrude","CAP_EDGE",EDGE,{"disambiguationData":[OSD([sQuery(id+"F14.wireOp",EDGE,"E113.0")])],"isStart":false});
            fillet(context, id + "F26", {"entities" : qUnion([Q0]), "radius" : 25.4 * mm, "tangentPropagation" : true, "allowEdgeOverflow" : false});
        }
        {
            var Q0;
            Q0=makeQuery(id+"F15.boolean.opBoolean","MERGE",EDGE,{"derivedFrom":[makeQuery(id+"F1.opExtrude","SWEPT_EDGE",EDGE,{"disambiguationData":[OSD([sQuery(id+"F0.wireOp",EDGE,"E2"),sQuery(id+"F0.wireOp",EDGE,"E3")])]}),makeQuery(id+"F15.opExtrude","SWEPT_EDGE",EDGE,{"disambiguationData":[OSD([sQuery(id+"F14.wireOp",EDGE,"E110.0"),sQuery(id+"F14.wireOp",EDGE,"E116.0")])]})]});
            var Q1;
            Q1=makeQuery(id+"F13.boolean.opBoolean","MERGE",EDGE,{"derivedFrom":[makeQuery(id+"F11.opPattern","COPY",EDGE,{"derivedFrom":makeQuery(id+"F1.opExtrude","SWEPT_EDGE",EDGE,{"disambiguationData":[OSD([sQuery(id+"F0.wireOp",EDGE,"E2"),sQuery(id+"F0.wireOp",EDGE,"E3")])]}),"instanceName":"1"}),makeQuery(id+"F13.opExtrude","SWEPT_EDGE",EDGE,{"disambiguationData":[OSD([sQuery(id+"F12.wireOp",EDGE,"E103.0"),sQuery(id+"F12.wireOp",EDGE,"E104.0")])]})]});
            fillet(context, id + "F27", {"entities" : qUnion([Q0, Q1]), "radius" : 50.8 * mm, "tangentPropagation" : true, "allowEdgeOverflow" : false});
        }
        {
            var Q0;
            Q0=makeQuery(id+"F13.boolean.opBoolean","MERGE",EDGE,{"derivedFrom":[makeQuery(id+"F11.opPattern","COPY",EDGE,{"derivedFrom":makeQuery(id+"F1.opExtrude","SWEPT_EDGE",EDGE,{"disambiguationData":[OSD([sQuery(id+"F0.wireOp",EDGE,"E5"),sQuery(id+"F0.wireOp",EDGE,"E6")])]}),"instanceName":"1"}),makeQuery(id+"F13.opExtrude","SWEPT_EDGE",EDGE,{"disambiguationData":[OSD([sQuery(id+"F12.wireOp",EDGE,"E105.0"),sQuery(id+"F12.wireOp",EDGE,"E106.0")])]})]});
            var Q1;
            Q1=makeQuery(id+"F15.boolean.opBoolean","MERGE",EDGE,{"derivedFrom":[makeQuery(id+"F1.opExtrude","SWEPT_EDGE",EDGE,{"disambiguationData":[OSD([sQuery(id+"F0.wireOp",EDGE,"E5"),sQuery(id+"F0.wireOp",EDGE,"E6")])]}),makeQuery(id+"F15.opExtrude","SWEPT_EDGE",EDGE,{"disambiguationData":[OSD([sQuery(id+"F14.wireOp",EDGE,"E112.0"),sQuery(id+"F14.wireOp",EDGE,"E113.0")])]})]});
            fillet(context, id + "F28", {"entities" : qUnion([Q0, Q1]), "radius" : 50.8 * mm, "tangentPropagation" : true, "allowEdgeOverflow" : false});
        }
    });
